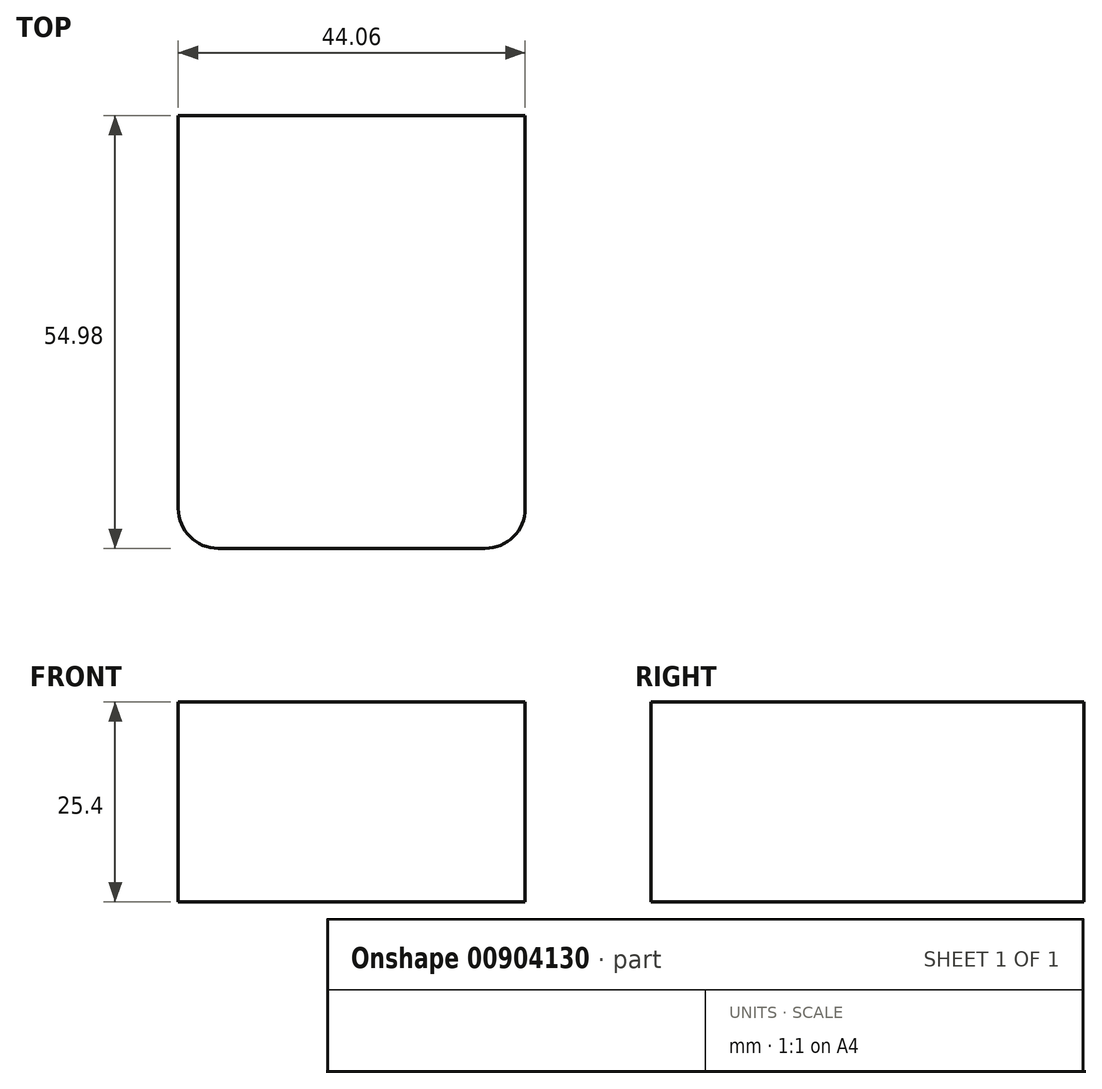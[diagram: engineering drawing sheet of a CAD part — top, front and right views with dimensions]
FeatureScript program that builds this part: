
annotation { "Feature Type Name" : "Feature", "Feature Type Description" : "" }
export const myFeature = defineFeature(function(context is Context, id is Id, definition is map)
    precondition{}
    {
        {
            var Q0;
            Q0=qCreatedBy(makeId("Top.planeOp"),FACE);
            var sketch = newSketch(context, id + "F0", { "sketchPlane" : qUnion([Q0])});
            skLineSegment(sketch, "E0.bottom", {"start": v(22.03, -27.5) * mm, "end": v(-22.03, -27.5) * mm});
            skLineSegment(sketch, "E0.top", {"start": v(22.03, 27.5) * mm, "end": v(-22.03, 27.5) * mm});
            skLineSegment(sketch, "E0.left", {"start": v(22.03, -27.5) * mm, "end": v(22.03, 27.5) * mm});
            skLineSegment(sketch, "E0.right", {"start": v(-22.03, -27.5) * mm, "end": v(-22.03, 27.5) * mm});
            skPoint(sketch, "E0.middle", {"position": v(0, 0) * mm});
            skSolve(sketch);
        }
        {
            var Q0;
            Q0=makeQuery(id+"F0.imprint","IMPRINT",FACE,{"disambiguationData":[TD([[makeQuery(id+"F0.imprint","IMPRINT",EDGE,{"derivedFrom":sQuery(id+"F0.wireOp",EDGE,"E0.bottom")}),-1.0]])]});
            extrude(context, id + "F1", {"entities" : qUnion([Q0]), "depth" : 25.4 * mm, "offsetDistance" : 25.4 * mm});
        }
        {
            var Q0;
            Q0=makeQuery(id+"F1.opExtrude","SWEPT_EDGE",EDGE,{"disambiguationData":[OSD([sQuery(id+"F0.wireOp",EDGE,"E0.bottom"),sQuery(id+"F0.wireOp",EDGE,"E0.right")])]});
            var Q1;
            Q1=makeQuery(id+"F1.opExtrude","SWEPT_EDGE",EDGE,{"disambiguationData":[OSD([sQuery(id+"F0.wireOp",EDGE,"E0.bottom"),sQuery(id+"F0.wireOp",EDGE,"E0.left")])]});
            fillet(context, id + "F2", {"entities" : qUnion([Q0, Q1]), "radius" : 5.08 * mm, "tangentPropagation" : true, "allowEdgeOverflow" : false});
        }
    });
